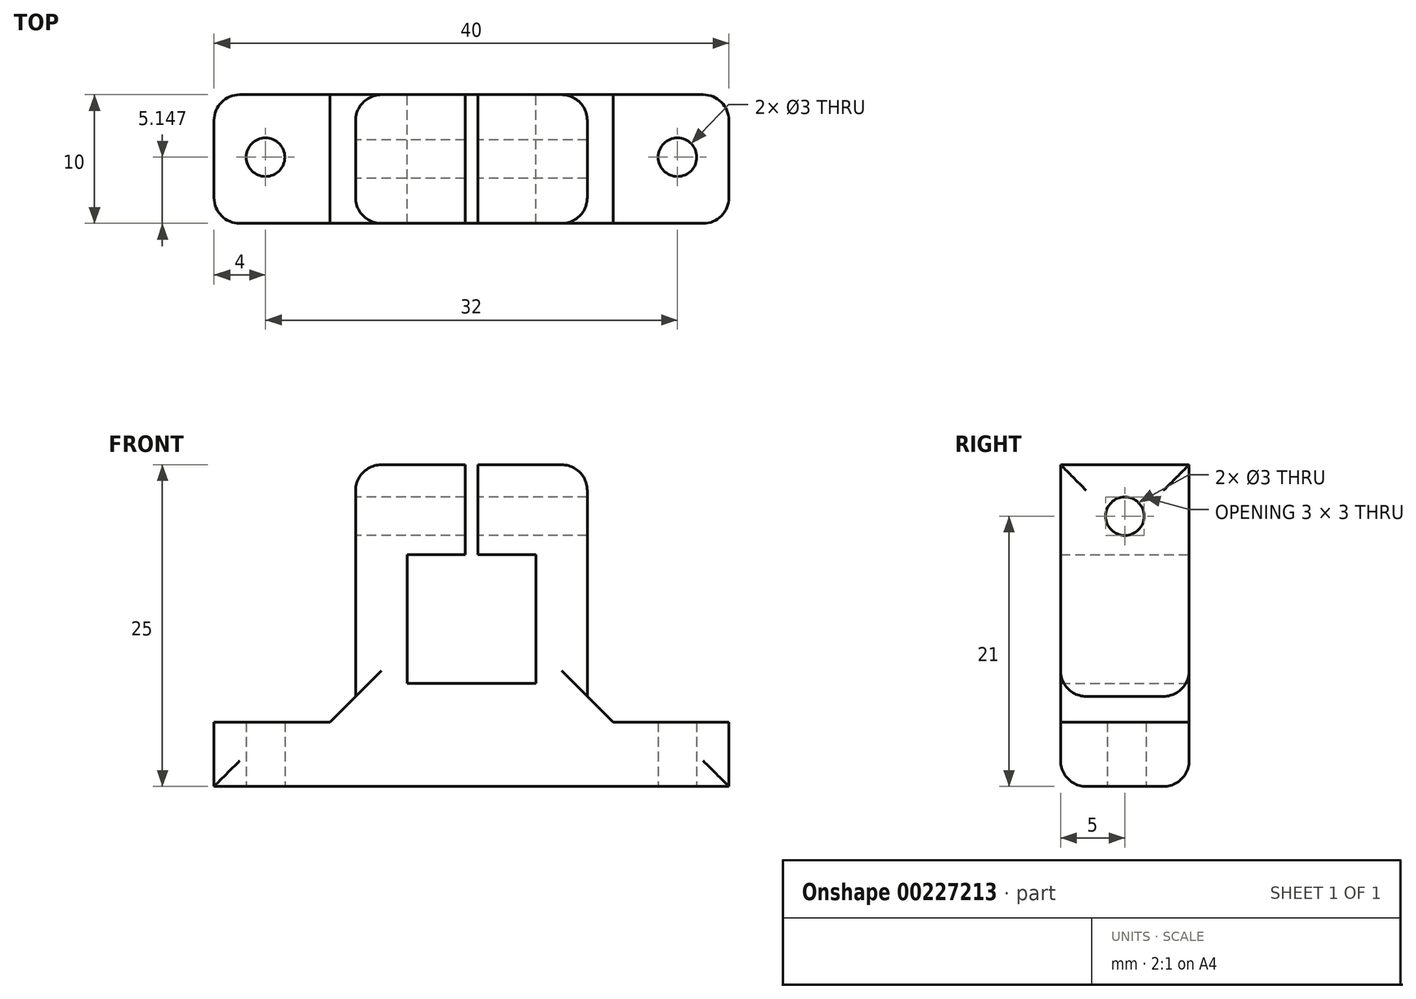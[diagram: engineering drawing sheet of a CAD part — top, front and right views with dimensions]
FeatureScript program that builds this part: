
annotation { "Feature Type Name" : "Feature", "Feature Type Description" : "" }
export const myFeature = defineFeature(function(context is Context, id is Id, definition is map)
    precondition{}
    {
        {
            var Q0;
            Q0=qCreatedBy(makeId("Front.planeOp"),FACE);
            var sketch = newSketch(context, id + "F0", { "sketchPlane" : qUnion([Q0])});
            skLineSegment(sketch, "E0.bottom", {"start": v(20, -11.5) * mm, "end": v(-20, -11.5) * mm});
            skLineSegment(sketch, "E0.top", {"start": v(9, 11.5) * mm, "end": v(-9, 11.5) * mm});
            skLineSegment(sketch, "E0.left", {"start": v(20, -11.5) * mm, "end": v(20, -6.5) * mm});
            skLineSegment(sketch, "E0.right", {"start": v(-20, -11.5) * mm, "end": v(-20, -6.5) * mm});
            skPoint(sketch, "E0.middle", {"position": v(0, 0) * mm});
            skLineSegment(sketch, "E1", {"start": v(-20, -6.5) * mm, "end": v(-9, -6.5) * mm});
            skLineSegment(sketch, "E2", {"start": v(-9, -6.5) * mm, "end": v(-9, 11.5) * mm});
            skLineSegment(sketch, "E3.MirrorCS", {"start": v(9, -6.5) * mm, "end": v(9, 11.5) * mm});
            skPoint(sketch, "E4.orphan", {"position": v(-20, 11.5) * mm});
            skLineSegment(sketch, "E5.trimOffspring", {"start": v(9, -6.5) * mm, "end": v(20, -6.5) * mm});
            skPoint(sketch, "E6.orphan", {"position": v(20, 11.5) * mm});
            skPoint(sketch, "E7.start.orphan", {"position": v(-0.5, 11.5) * mm});
            skPoint(sketch, "E8.orphan", {"position": v(-1.34, 4.87) * mm});
            skPoint(sketch, "E9.MirrorCS.start.orphan", {"position": v(0.5, 11.5) * mm});
            skPoint(sketch, "E10.start.orphan", {"position": v(1.34, 4.87) * mm});
            skLineSegment(sketch, "E11.bottom", {"start": v(5, -3.5) * mm, "end": v(-5, -3.5) * mm});
            skLineSegment(sketch, "E11.top", {"start": v(5, 6.5) * mm, "end": v(-5, 6.5) * mm});
            skLineSegment(sketch, "E11.left", {"start": v(5, -3.5) * mm, "end": v(5, 6.5) * mm});
            skLineSegment(sketch, "E11.right", {"start": v(-5, -3.5) * mm, "end": v(-5, 6.5) * mm});
            skPoint(sketch, "E11.middle", {"position": v(0, 1.5) * mm});
            skLineSegment(sketch, "E12", {"start": v(-0.5, 11.5) * mm, "end": v(-0.5, 6.5) * mm});
            skLineSegment(sketch, "E13.MirrorCS", {"start": v(0.5, 11.5) * mm, "end": v(0.5, 6.5) * mm});
            skSolve(sketch);
        }
        {
            var Q0;
            Q0=makeQuery(id+"F0.imprint","IMPRINT",FACE,{"disambiguationData":[TD([[makeQuery(id+"F0.imprint","IMPRINT",EDGE,{"derivedFrom":sQuery(id+"F0.wireOp",EDGE,"E0.bottom")}),-1.0]])]});
            extrude(context, id + "F1", {"entities" : qUnion([Q0]), "depth" : 10 * mm});
        }
        {
            var Q0;
            Q0=makeQuery(id+"F1.opExtrude","SWEPT_FACE",FACE,{"disambiguationData":[OSD([sQuery(id+"F0.wireOp",EDGE,"E0.bottom")])]});
            var sketch = newSketch(context, id + "F2", { "sketchPlane" : qUnion([Q0])});
            skCircle(sketch, "E14", {"center": v(16, 4.85) * mm, "radius": 1.5 * mm});
            skCircle(sketch, "E15.MirrorC", {"center": v(-16, 4.85) * mm, "radius": 1.5 * mm});
            skSolve(sketch);
        }
        {
            var Q0;
            Q0 = qSketchRegion(id + "F2", true);
            extrude(context, id + "F3", {"entities" : qUnion([Q0]), "operationType" : NewBodyOperationType.REMOVE, "oppositeDirection" : true, "depth" : 10.5 * mm});
        }
        {
            var Q0;
            Q0=makeQuery(id+"F1.opExtrude","SWEPT_FACE",FACE,{"disambiguationData":[OSD([sQuery(id+"F0.wireOp",EDGE,"E2")])]});
            var sketch = newSketch(context, id + "F4", { "sketchPlane" : qUnion([Q0])});
            skCircle(sketch, "E16", {"center": v(5, 9.5) * mm, "radius": 1.5 * mm});
            skSolve(sketch);
        }
        {
            var Q0;
            Q0 = qSketchRegion(id + "F4", true);
            extrude(context, id + "F5", {"entities" : qUnion([Q0]), "operationType" : NewBodyOperationType.REMOVE, "oppositeDirection" : true, "depth" : 25 * mm});
        }
        {
            var Q0;
            {var subQ0=sQuery(id+"F0.wireOp",EDGE,"E0.top");Q0=makeQuery(id+"F1.opExtrude","SWEPT_FACE",FACE,{"disambiguationData":[OSD([subQ0]),TDD([makeQuery(id+"F0.imprint","IMPRINT",EDGE,{"disambiguationData":[TD([[makeQuery(id+"F0.imprint","INTERSECT",VERTEX,{"derivedFrom":[subQ0,sQuery(id+"F0.wireOp",EDGE,"E3.MirrorCS")]}),-1.0]])],"derivedFrom":subQ0})])]});}
            var Q1;
            {var subQ0=sQuery(id+"F0.wireOp",EDGE,"E0.top");Q1=makeQuery(id+"F1.opExtrude","SWEPT_FACE",FACE,{"disambiguationData":[OSD([subQ0]),TDD([makeQuery(id+"F0.imprint","IMPRINT",EDGE,{"disambiguationData":[TD([[makeQuery(id+"F0.imprint","INTERSECT",VERTEX,{"derivedFrom":[subQ0,sQuery(id+"F0.wireOp",EDGE,"E2")]}),1.0]])],"derivedFrom":subQ0})])]});}
            extrude(context, id + "F6", {"entities" : qUnion([Q0, Q1]), "operationType" : NewBodyOperationType.ADD, "depth" : 2 * mm});
        }
        {
            var Q0;
            Q0=makeQuery(id+"F1.opExtrude","SWEPT_EDGE",EDGE,{"disambiguationData":[OSD([sQuery(id+"F0.wireOp",EDGE,"E1"),sQuery(id+"F0.wireOp",EDGE,"E2")])]});
            chamfer(context, id + "F7", {"entities" : qUnion([Q0]), "width" : 2 * mm, "tangentPropagation" : true});
        }
        {
            var Q0;
            Q0=makeQuery(id+"F1.opExtrude","SWEPT_EDGE",EDGE,{"disambiguationData":[OSD([sQuery(id+"F0.wireOp",EDGE,"E3.MirrorCS"),sQuery(id+"F0.wireOp",EDGE,"E5.trimOffspring")])]});
            chamfer(context, id + "F8", {"entities" : qUnion([Q0]), "width" : 2 * mm, "tangentPropagation" : true});
        }
        {
            var Q0;
            Q0=makeQuery(id+"F1.opExtrude","CAP_EDGE",EDGE,{"disambiguationData":[OSD([sQuery(id+"F0.wireOp",EDGE,"E0.right")])],"isStart":false});
            var Q1;
            Q1=makeQuery(id+"F1.opExtrude","CAP_EDGE",EDGE,{"disambiguationData":[OSD([sQuery(id+"F0.wireOp",EDGE,"E0.right")])],"isStart":true});
            var Q2;
            Q2=makeQuery(id+"F1.opExtrude","CAP_EDGE",EDGE,{"disambiguationData":[OSD([sQuery(id+"F0.wireOp",EDGE,"E0.left")])],"isStart":true});
            var Q3;
            Q3=makeQuery(id+"F1.opExtrude","CAP_EDGE",EDGE,{"disambiguationData":[OSD([sQuery(id+"F0.wireOp",EDGE,"E0.left")])],"isStart":false});
            var Q4;
            Q4=makeQuery(id+"F6.opExtrude","CAP_EDGE",EDGE,{"disambiguationData":[OSD([sQuery(id+"F0.wireOp",EDGE,"E0.top"),sQuery(id+"F0.wireOp",EDGE,"E3.MirrorCS")])],"isStart":false});
            var Q5;
            Q5=makeQuery(id+"F6.opExtrude","CAP_EDGE",EDGE,{"disambiguationData":[OSD([sQuery(id+"F0.wireOp",EDGE,"E0.top"),sQuery(id+"F0.wireOp",EDGE,"E2")])],"isStart":false});
            var Q6;
            {var subQ0=sQuery(id+"F0.wireOp",EDGE,"E2");var subQ1=sQuery(id+"F0.wireOp",EDGE,"E0.top");Q6=makeQuery(id+"F6.boolean.opBoolean","MERGE",EDGE,{"derivedFrom":[makeQuery(id+"F1.opExtrude","CAP_EDGE",EDGE,{"disambiguationData":[OSD([subQ0])],"isStart":false}),makeQuery(id+"F6.opExtrude","SWEPT_EDGE",EDGE,{"disambiguationData":[OSD([subQ1,subQ0]),TDD([makeQuery(id+"F1.opExtrude","CAP_VERTEX",VERTEX,{"disambiguationData":[OSD([subQ1,subQ0])],"isStart":false})])]})]});}
            var Q7;
            {var subQ0=sQuery(id+"F0.wireOp",EDGE,"E3.MirrorCS");var subQ1=sQuery(id+"F0.wireOp",EDGE,"E0.top");Q7=makeQuery(id+"F6.boolean.opBoolean","MERGE",EDGE,{"derivedFrom":[makeQuery(id+"F1.opExtrude","CAP_EDGE",EDGE,{"disambiguationData":[OSD([subQ0])],"isStart":false}),makeQuery(id+"F6.opExtrude","SWEPT_EDGE",EDGE,{"disambiguationData":[OSD([subQ1,subQ0]),TDD([makeQuery(id+"F1.opExtrude","CAP_VERTEX",VERTEX,{"disambiguationData":[OSD([subQ1,subQ0])],"isStart":false})])]})]});}
            var Q8;
            {var subQ0=sQuery(id+"F0.wireOp",EDGE,"E3.MirrorCS");var subQ1=sQuery(id+"F0.wireOp",EDGE,"E0.top");Q8=makeQuery(id+"F6.boolean.opBoolean","MERGE",EDGE,{"derivedFrom":[makeQuery(id+"F1.opExtrude","CAP_EDGE",EDGE,{"disambiguationData":[OSD([subQ0])],"isStart":true}),makeQuery(id+"F6.opExtrude","SWEPT_EDGE",EDGE,{"disambiguationData":[OSD([subQ1,subQ0]),TDD([makeQuery(id+"F1.opExtrude","CAP_VERTEX",VERTEX,{"disambiguationData":[OSD([subQ1,subQ0])],"isStart":true})])]})]});}
            var Q9;
            {var subQ0=sQuery(id+"F0.wireOp",EDGE,"E2");var subQ1=sQuery(id+"F0.wireOp",EDGE,"E0.top");Q9=makeQuery(id+"F6.boolean.opBoolean","MERGE",EDGE,{"derivedFrom":[makeQuery(id+"F1.opExtrude","CAP_EDGE",EDGE,{"disambiguationData":[OSD([subQ0])],"isStart":true}),makeQuery(id+"F6.opExtrude","SWEPT_EDGE",EDGE,{"disambiguationData":[OSD([subQ1,subQ0]),TDD([makeQuery(id+"F1.opExtrude","CAP_VERTEX",VERTEX,{"disambiguationData":[OSD([subQ1,subQ0])],"isStart":true})])]})]});}
            var Q10;
            Q10=makeQuery(id+"F1.opExtrude","CAP_EDGE",EDGE,{"disambiguationData":[OSD([sQuery(id+"F0.wireOp",EDGE,"E0.bottom")])],"isStart":true});
            var Q11;
            Q11=makeQuery(id+"F1.opExtrude","CAP_EDGE",EDGE,{"disambiguationData":[OSD([sQuery(id+"F0.wireOp",EDGE,"E0.bottom")])],"isStart":false});
            fillet(context, id + "F9", {"entities" : qUnion([Q0, Q1, Q2, Q3, Q4, Q5, Q6, Q7, Q8, Q9, Q10, Q11]), "radius" : 2 * mm, "tangentPropagation" : true, "allowEdgeOverflow" : false});
        }
    });
